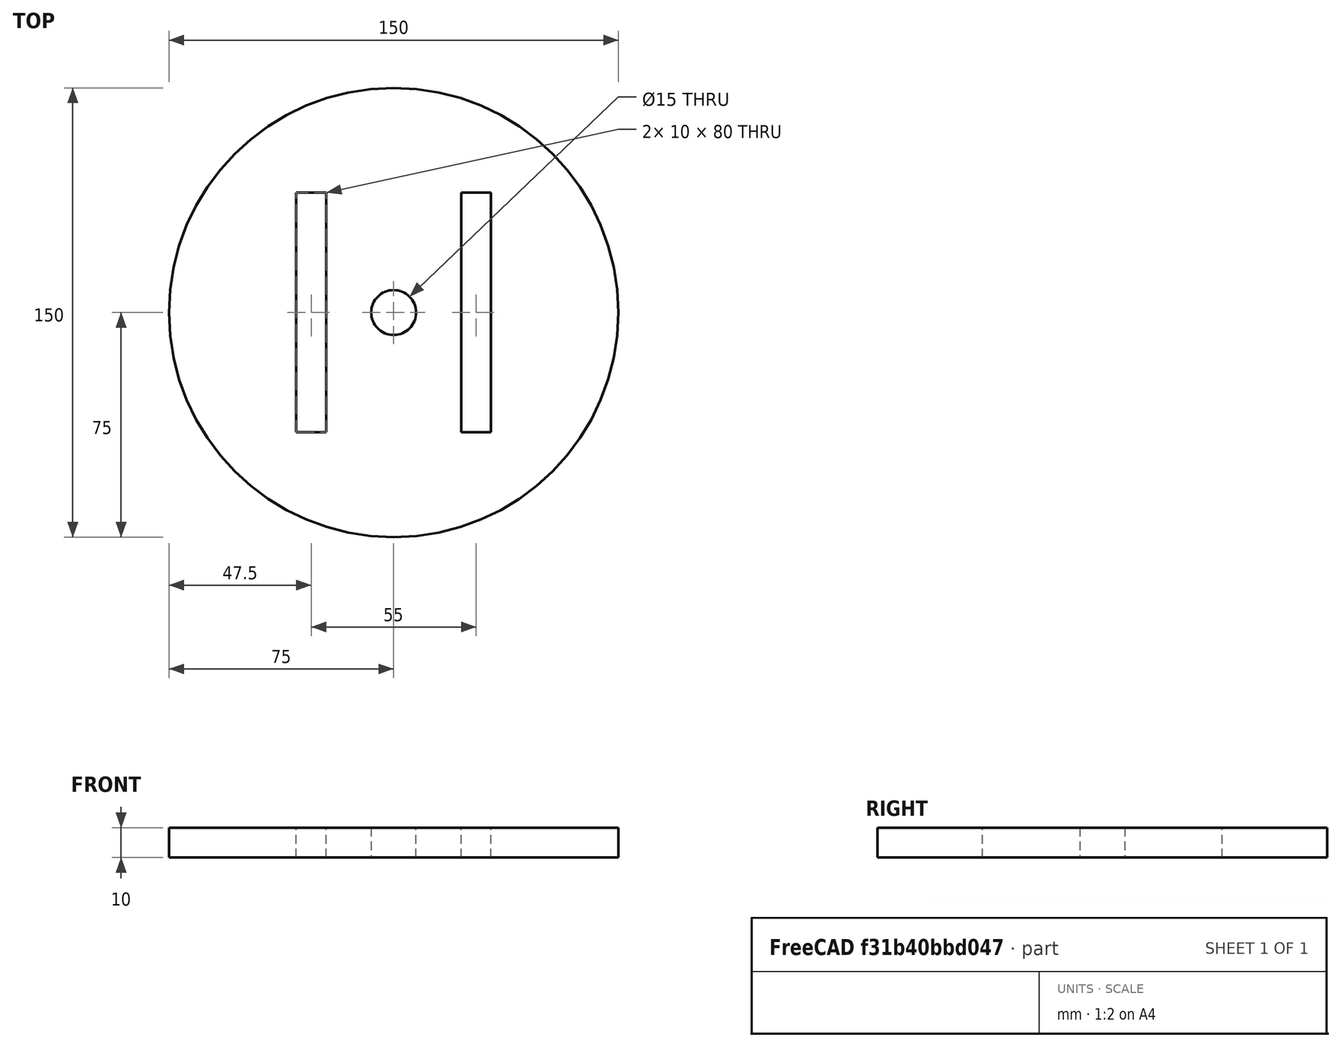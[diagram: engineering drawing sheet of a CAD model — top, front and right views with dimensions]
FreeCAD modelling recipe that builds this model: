
FCSTD DOCUMENT  (FreeCAD 0.18R4 (GitTag))
Label: rotaryBase
License: All rights reserved
LicenseURL: http://en.wikipedia.org/wiki/All_rights_reserved
objects: Drawing::FeatureViewPart×3, App::Part×1, Sketcher::SketchObject×1, PartDesign::Pad×1, PartDesign::Body×1, Drawing::FeaturePage×1, Part::Feature×1
note: 5 computed .brp shape members not serialized (recipe doc carries the construction recipe); baked Part::Feature solids carry a one-line shape summary decoded from their .brp

FEATURE [App::Part] Part
  Origin = -> Origin
FEATURE [Sketcher::SketchObject] Sketch
  MapMode = 5
  Support = -> [XY_Plane001]
  sketch-geometry (10):
    g0: Circle CenterX=0 CenterY=0 CenterZ=0 NormalX=0 NormalY=0 NormalZ=1 AngleXU=0 Radius=75
    g1: Circle CenterX=0 CenterY=0 CenterZ=0 NormalX=0 NormalY=0 NormalZ=1 AngleXU=0 Radius=7.5
    g2: LineSegment StartX=-32.5 StartY=40 StartZ=0 EndX=-22.5 EndY=40 EndZ=0
    g3: LineSegment StartX=-22.5 StartY=40 StartZ=0 EndX=-22.5 EndY=-40 EndZ=0
    g4: LineSegment StartX=-22.5 StartY=-40 StartZ=0 EndX=-32.5 EndY=-40 EndZ=0
    g5: LineSegment StartX=-32.5 StartY=-40 StartZ=0 EndX=-32.5 EndY=40 EndZ=0
    g6: LineSegment StartX=22.5 StartY=40 StartZ=0 EndX=32.5 EndY=40 EndZ=0
    g7: LineSegment StartX=32.5 StartY=40 StartZ=0 EndX=32.5 EndY=-40 EndZ=0
    g8: LineSegment StartX=32.5 StartY=-40 StartZ=0 EndX=22.5 EndY=-40 EndZ=0
    g9: LineSegment StartX=22.5 StartY=-40 StartZ=0 EndX=22.5 EndY=40 EndZ=0
  constraints (27):
    c: Coincident(g0,g-1)
    c: Coincident(g1,g0)
    c: Diameter(g1) = 15
    c: Diameter(g0) = 150
    c: Coincident(g2,g3)
    c: Coincident(g3,g4)
    c: Coincident(g4,g5)
    c: Coincident(g5,g2)
    c: Horizontal(g2)
    c: Horizontal(g4)
    c: Vertical(g3)
    c: Vertical(g5)
    c: Coincident(g6,g7)
    c: Coincident(g7,g8)
    c: Coincident(g8,g9)
    c: Coincident(g9,g6)
    c: Horizontal(g6)
    c: Horizontal(g8)
    c: Vertical(g7)
    c: DistanceY(g7,g7) = 80
    c: Symmetric(g8,g6,g-1)
    c: Horizontal(g6,g2)
    c: Horizontal(g3,g8)
    c: DistanceX(g4,g4) = 10
    c: DistanceX(g8,g8) = 10
    c: DistanceX(g0,g6) = 22.5
    c: DistanceX(g2,g0) = 22.5
FEATURE [PartDesign::Pad] Pad
  Length = 10
  Length2 = 100
  Profile = -> Sketch
  Type = 0
FEATURE [PartDesign::Body] Body
  Group = -> [Sketch,Pad]
  Origin = -> Origin001
  Tip = -> Pad
FEATURE [Drawing::FeatureViewPart] Ortho  label="Ortho_0_0"
  Direction = (1,0,0)
  HiddenWidth = 0.15
  LineWidth = 0.35
  Rotation = -90
  ShowHiddenLines = true
  ShowSmoothLines = false
  Source = -> Body
  Tolerance = 0.05
  ViewResult = <blob: 3986 chars omitted>
  Visible = false
  X = 118.333
  Y = 208
FEATURE [Drawing::FeatureViewPart] Ortho001  label="Ortho_1_1"
  Direction = (0.57735,0.57735,0.57735)
  HiddenWidth = 0.15
  LineWidth = 0.35
  Rotation = 120
  ShowHiddenLines = true
  ShowSmoothLines = false
  Source = -> Body
  Tolerance = 0.05
  ViewResult = <blob: 3537 chars omitted>
  Visible = false
  X = 301.667
  Y = 108.082
FEATURE [Drawing::FeatureViewPart] Ortho002  label="Ortho_0_1"
  Direction = (0,0,1)
  HiddenWidth = 0.15
  LineWidth = 0.35
  Rotation = 90
  ShowHiddenLines = true
  ShowSmoothLines = false
  Source = -> Body
  Tolerance = 0.05
  ViewResult = <g id="Ortho_0_1"\n   transform="rotate(90,118.333,104) translate(118.333,104) scale(1,1)"\n  >\n<g   fill="none"\n   stroke="rgb(0, 0, 0)"\n   stroke-dasharray="0.2,0.1)"\n   stroke-linecap="butt"\n   stroke-linejoin="miter"\n   stroke-width="0.150000"\n   transform="scale(1,-1)"\n  >\n<circle cx ="0" cy ="0" r ="75" /><path id= "2" d=" M 22.5 40 L 32.5 40 " />\n<path id= "3" d=" M 32.5 40 L 32.5 -40 " />\n<path id= "4" d=" M 32.5 -40 L 22.5 -40 " />\n<path id= "5" d=" M 22.5 -40 L 22.5 40 " />\n<path id= "6" d=" M -32.5 40 L -22.5 40 " />\n<path id= "7" d=" M -22.5 40 L -22.5 -40 " />\n<path id= "8" d=" M -22.5 -40 L -32.5 -40 " />\n<path id= "9" d=" M -32.5 -40 L -32.5 40 " />\n<circle cx ="0" cy ="0" r ="7.5" /></g>\n<g   fill="none"\n   stroke="rgb(0, 0, 0)"\n   stroke-linecap="butt"\n   stroke-linejoin="miter"\n   stroke-width="0.350000"\n   transform="scale(1,-1)"\n  >\n<circle cx ="0" cy ="0" r ="75" /><path id= "2" d=" M 22.5 40 L 32.5 40 " />\n<path id= "3" d=" M 32.5 40 L 32.5 -40 " />\n<path id= "4" d=" M 32.5 -40 L 22.5 -40 " />\n<path id= "5" d=" M 22.5 -40 L 22.5 40 " />\n<path id= "6" d=" M -32.5 40 L -22.5 40 " />\n<path id= "7" d=" M -22.5 40 L -22.5 -40 " />\n<path id= "8" d=" M -22.5 -40 L -32.5 -40 " />\n<path id= "9" d=" M -32.5 -40 L -32.5 40 " />\n<circle cx ="0" cy ="0" r ="7.5" /></g>\n</g>
  Visible = false
  X = 118.333
  Y = 104
FEATURE [Drawing::FeaturePage] Page
  EditableTexts = L. Cañamar Amaya | March 19, 2021 | A. A. Pech Che | 1:1 | 6 | 1 | Rotary Base | rotating base platform
  Group = -> [Ortho,Ortho001,Ortho002]
  Template = D:/Installed Programs/FreeCAD 0.18/data/Mod/Drawing/Templates/A3_Landscape.svg
FEATURE [Part::Feature] Pad001  label="Robot_RotaryBase"
  shape: bbox 150 x 150 x 10 mm, 12 faces (baked)
